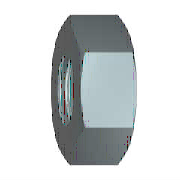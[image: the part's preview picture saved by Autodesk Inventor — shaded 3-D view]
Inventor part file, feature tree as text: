
AUTODESK INVENTOR PART (.ipt)
format: ipt  version: 2022.1 (Build 261234000, 234)  size: 164,352 bytes
history: native  units: mm (DEFAULTED — no unit token found)
features: sketch x3, extrude x1, chamfer x1, hole x1, other x1, plane x1
ambient origin geometry x7: Origin, YZ Plane, XZ Plane, X Axis, Y Axis, Z Axis, Center Point
bodies: Solid1 (feature_tree)
feature tree (8):
  extrude  "Cuerpo"  Depth=6.8mm
  chamfer  "Chaflán1"  Angle=30.0deg  [1 undecoded]
  hole  "Rosca"  [1 undecoded]
  other  "Work Axis1"
  plane  "Work Plane1"
  sketch  "Boceto1"  dims[d0=15.011107mm d1=6.8mm]
  sketch  "Boceto2"  dims[d2=0.0mm]
  sketch  "Boceto3"  dims[d3=30.0deg d4=30.0deg d5=11.6mm d6=11.6mm d7=90.0deg d25=6.647mm d26=6.0mm d27=4.0mm d28=2.0mm d29=14.3117mm d30=8.0mm d31=20.594885mm d8=0.676582mm d9=30.0deg d10=0.676582mm d11=30.0deg d13=0.0mm d14=0.0mm d39=0.0mm d40=0.676582mm d41=0.676582mm d42=0.0mm]
note: 2 required parameter values undecoded (feature->parameter linkage not recoverable at this tier; creation-order binding heuristic only, values carry confidence <= 0.55)
